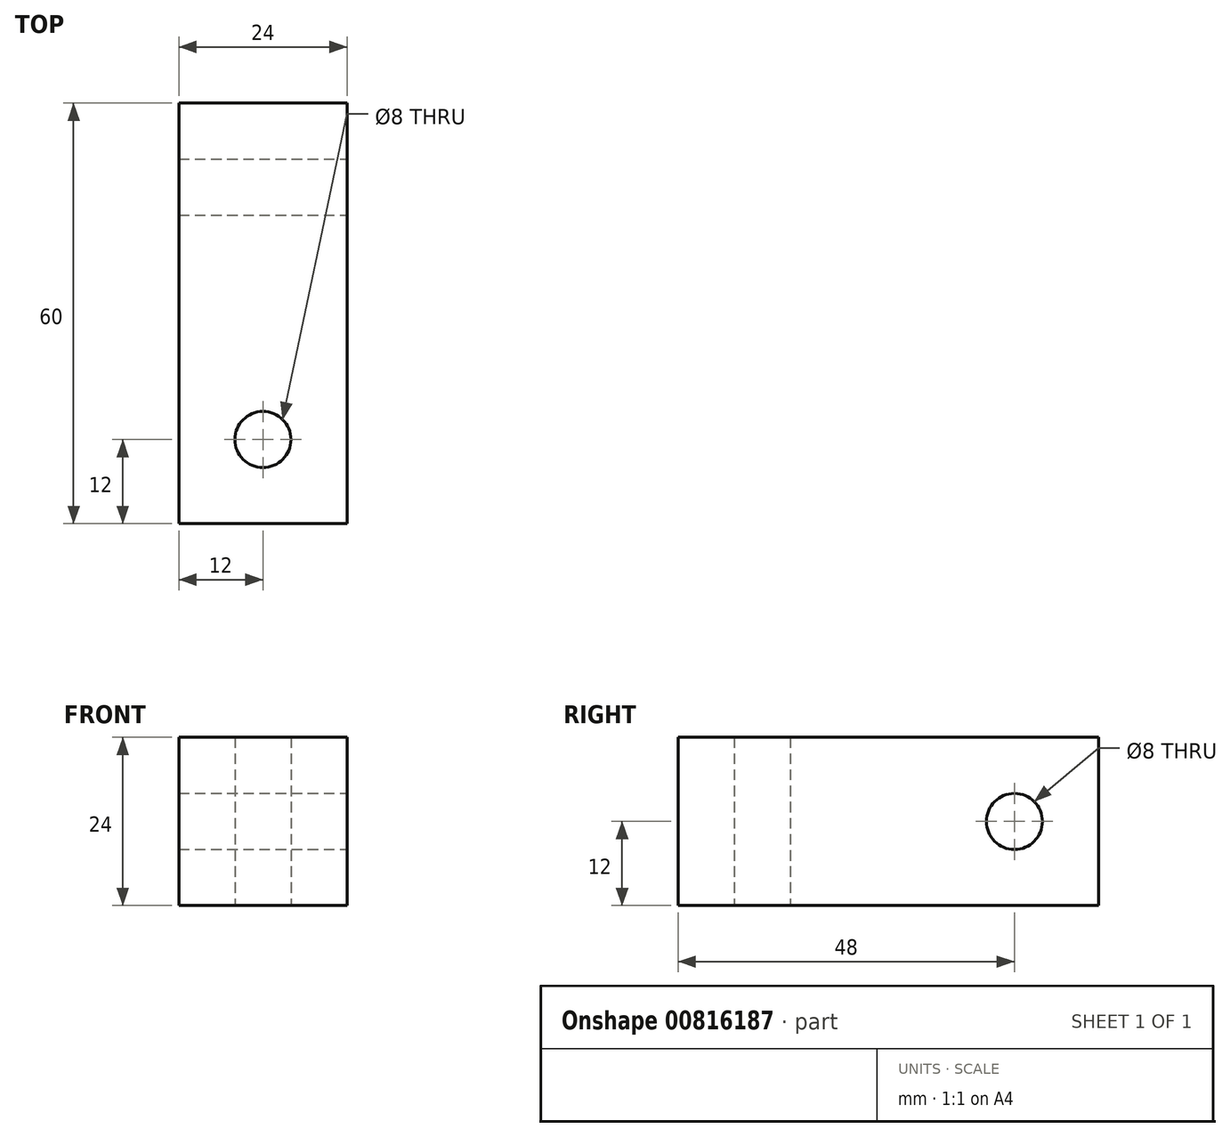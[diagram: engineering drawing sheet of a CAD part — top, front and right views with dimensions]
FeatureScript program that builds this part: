
annotation { "Feature Type Name" : "Feature", "Feature Type Description" : "" }
export const myFeature = defineFeature(function(context is Context, id is Id, definition is map)
    precondition{}
    {
        {
            var Q0;
            Q0=qCreatedBy(makeId("Front.planeOp"),FACE);
            var sketch = newSketch(context, id + "F0", { "sketchPlane" : qUnion([Q0])});
            skLineSegment(sketch, "E0.bottom", {"start": v(12, 12) * mm, "end": v(-12, 12) * mm});
            skLineSegment(sketch, "E0.top", {"start": v(12, -12) * mm, "end": v(-12, -12) * mm});
            skLineSegment(sketch, "E0.left", {"start": v(12, 12) * mm, "end": v(12, -12) * mm});
            skLineSegment(sketch, "E0.right", {"start": v(-12, 12) * mm, "end": v(-12, -12) * mm});
            skPoint(sketch, "E0.middle", {"position": v(0, 0) * mm});
            skSolve(sketch);
        }
        {
            var Q0;
            Q0 = qSketchRegion(id + "F0", true);
            extrude(context, id + "F1", {"entities" : qUnion([Q0]), "depth" : 60 * mm, "offsetDistance" : 25 * mm});
        }
        {
            var Q0;
            Q0=makeQuery(id+"F1.opExtrude","SWEPT_FACE",FACE,{"disambiguationData":[OSD([sQuery(id+"F0.wireOp",EDGE,"E0.top")])]});
            var sketch = newSketch(context, id + "F2", { "sketchPlane" : qUnion([Q0])});
            skLineSegment(sketch, "E1.0.0", {"start": v(-12, 0) * mm, "end": v(12, 0) * mm});
            skLineSegment(sketch, "E1.0.1", {"start": v(12, 0) * mm, "end": v(12, 60) * mm});
            skLineSegment(sketch, "E1.0.2", {"start": v(12, 60) * mm, "end": v(-12, 60) * mm});
            skLineSegment(sketch, "E1.0.3", {"start": v(-12, 60) * mm, "end": v(-12, 0) * mm});
            skLineSegment(sketch, "E2", {"start": v(0, 48) * mm, "end": v(0, 60) * mm, "construction": true});
            skLineSegment(sketch, "E3", {"start": v(0, 48) * mm, "end": v(-12, 48) * mm, "construction": true});
            skSolve(sketch);
        }
        {
            var Q0;
            Q0=makeQuery(id+"F1.opExtrude","SWEPT_FACE",FACE,{"disambiguationData":[OSD([sQuery(id+"F0.wireOp",EDGE,"E0.left")])]});
            var sketch = newSketch(context, id + "F3", { "sketchPlane" : qUnion([Q0])});
            skLineSegment(sketch, "E4", {"start": v(-12, 0) * mm, "end": v(-12, 12) * mm, "construction": true});
            skLineSegment(sketch, "E5", {"start": v(-12, 0) * mm, "end": v(0, 0) * mm, "construction": true});
            skSolve(sketch);
        }
        {
            var Q0;
            Q0=sQuery(id+"F3.wireOp",VERTEX,"E4.start");
            var Q1;
            Q1=sQuery(id+"F2.wireOp",VERTEX,"E2.start");
            var Q2;
            Q2=makeQuery(id+"F1.opExtrude","SWEPT_BODY",BODY,{"disambiguationData":[OSD([sQuery(id+"F0.wireOp",EDGE,"E0.bottom"),sQuery(id+"F0.wireOp",EDGE,"E0.top"),sQuery(id+"F0.wireOp",EDGE,"E0.left"),sQuery(id+"F0.wireOp",EDGE,"E0.right")])]});
            hole(context, id + "F4", {"style" : HoleStyle.SIMPLE, "endStyle" : HoleEndStyle.THROUGH, "holeDiameter" : 8 * mm, "majorDiameter" : 5 * mm, "isTappedThrough" : true, "tappedDepth" : 12 * mm, "tapClearance" : 3, "startFromSketch" : true, "locations" : qUnion([Q0, Q1]), "scope" : qUnion([Q2])});
        }
    });
